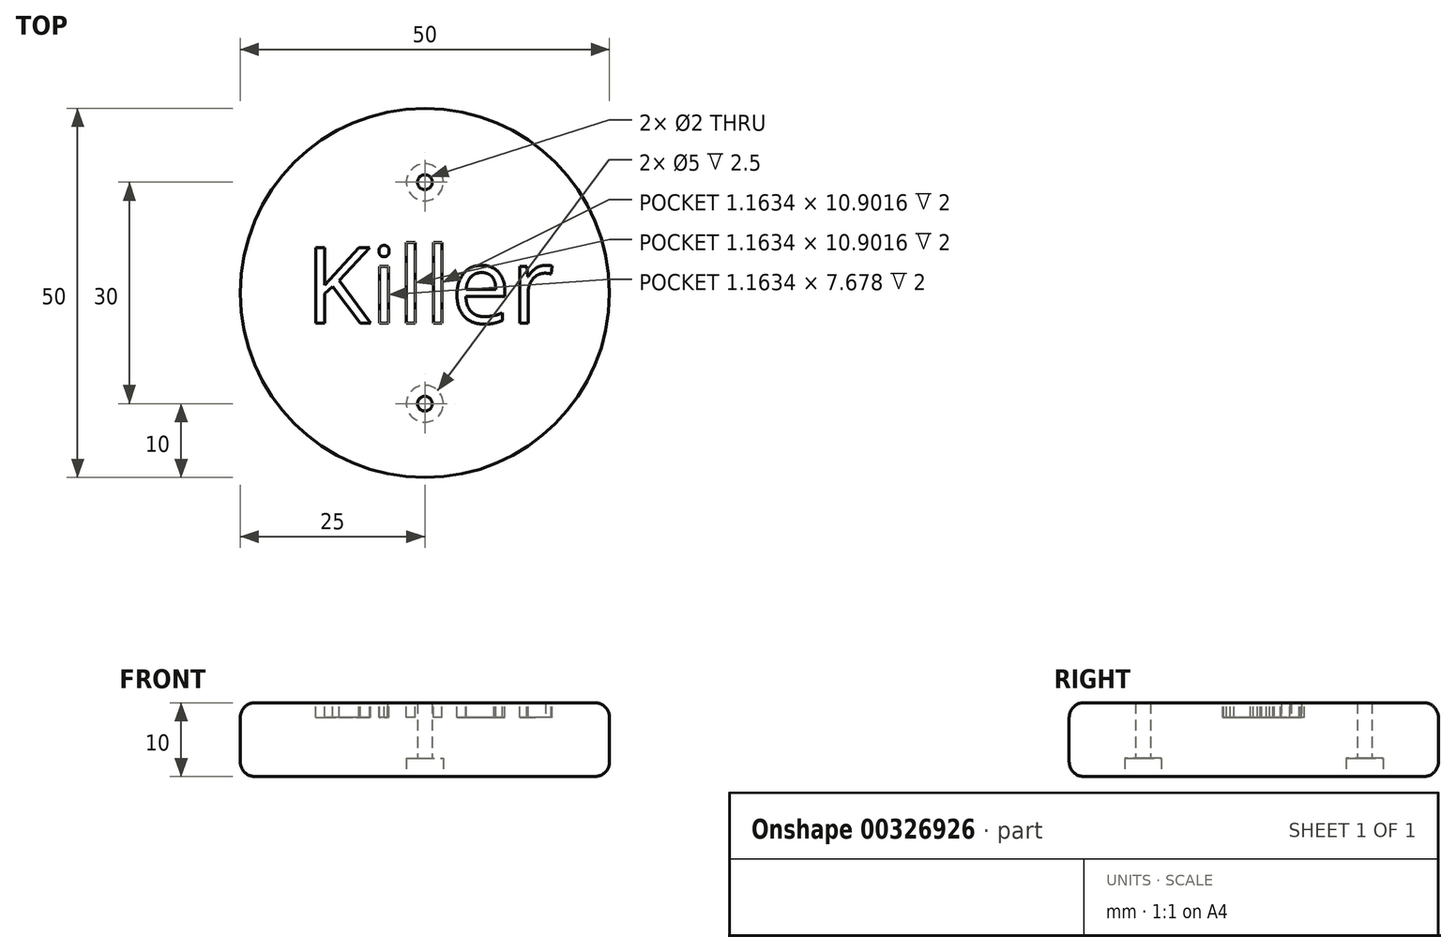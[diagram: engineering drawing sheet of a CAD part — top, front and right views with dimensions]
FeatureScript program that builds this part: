
annotation { "Feature Type Name" : "Feature", "Feature Type Description" : "" }
export const myFeature = defineFeature(function(context is Context, id is Id, definition is map)
    precondition{}
    {
        {
            var Q0;
            Q0=qCreatedBy(makeId("Top.planeOp"),FACE);
            var sketch = newSketch(context, id + "F0", { "sketchPlane" : qUnion([Q0])});
            skCircle(sketch, "E0", {"center": v(0, 0) * mm, "radius": 25 * mm});
            skSolve(sketch);
        }
        {
            var Q0;
            Q0=qSketchRegion(id+"F0",true);
            extrude(context, id + "F1", {"entities" : qUnion([Q0]), "depth" : 10 * mm});
        }
        {
            var Q0;
            Q0=makeQuery(id+"F1.opExtrude","CAP_EDGE",EDGE,{"disambiguationData":[OSD([sQuery(id+"F0.wireOp",EDGE,"E0")])],"isStart":false});
            var Q1;
            Q1=makeQuery(id+"F1.opExtrude","CAP_EDGE",EDGE,{"disambiguationData":[OSD([sQuery(id+"F0.wireOp",EDGE,"E0")])],"isStart":true});
            fillet(context, id + "F2", {"entities" : qUnion([Q0, Q1]), "radius" : 2 * mm, "tangentPropagation" : true, "allowEdgeOverflow" : false});
        }
        {
            var Q0;
            Q0=makeQuery(id+"F1.opExtrude","CAP_FACE",FACE,{"disambiguationData":[OSD([sQuery(id+"F0.wireOp",EDGE,"E0")])],"isStart":true});
            var sketch = newSketch(context, id + "F3", { "sketchPlane" : qUnion([Q0])});
            skPoint(sketch, "E1", {"position": v(0, 15) * mm});
            skPoint(sketch, "E2", {"position": v(0, -15) * mm});
            skSolve(sketch);
        }
        {
            var Q0;
            Q0=sQuery(id+"F3.wireOp",VERTEX,"E1");
            var Q1;
            Q1=sQuery(id+"F3.wireOp",VERTEX,"E2");
            var Q2;
            Q2=makeQuery(id+"F1.opExtrude","SWEPT_BODY",BODY,{"disambiguationData":[OSD([sQuery(id+"F0.wireOp",EDGE,"E0")])]});
            hole(context, id + "F4", {"style" : HoleStyle.C_BORE, "endStyle" : HoleEndStyle.THROUGH, "holeDiameter" : 2 * mm, "cBoreDiameter" : 5 * mm, "cBoreDepth" : 2.5 * mm, "startFromSketch" : true, "locations" : qUnion([Q0, Q1]), "scope" : qUnion([Q2]), "tappedDepth" : 12 * mm, "tapClearance" : 3});
        }
        {
            var Q0;
            Q0=makeQuery(id+"F1.opExtrude","CAP_FACE",FACE,{"disambiguationData":[OSD([sQuery(id+"F0.wireOp",EDGE,"E0")])],"isStart":false});
            var sketch = newSketch(context, id + "F5", { "sketchPlane" : qUnion([Q0])});
            skText(sketch, "E3", { "text": "Killer", "fontName": "OpenSans-Regular.ttf"});
            const initialGuessF5  = {"E3": [-0.01615, -0.00408, 1, 0, 0.01033]};
            skSetInitialGuess(sketch, initialGuessF5);
            skSolve(sketch);
        }
        {
            var Q0;
            Q0 = qSketchRegion(id + "F5", true);
            extrude(context, id + "F6", {"entities" : qUnion([Q0]), "operationType" : NewBodyOperationType.REMOVE, "oppositeDirection" : true, "depth" : 2 * mm});
        }
    });
